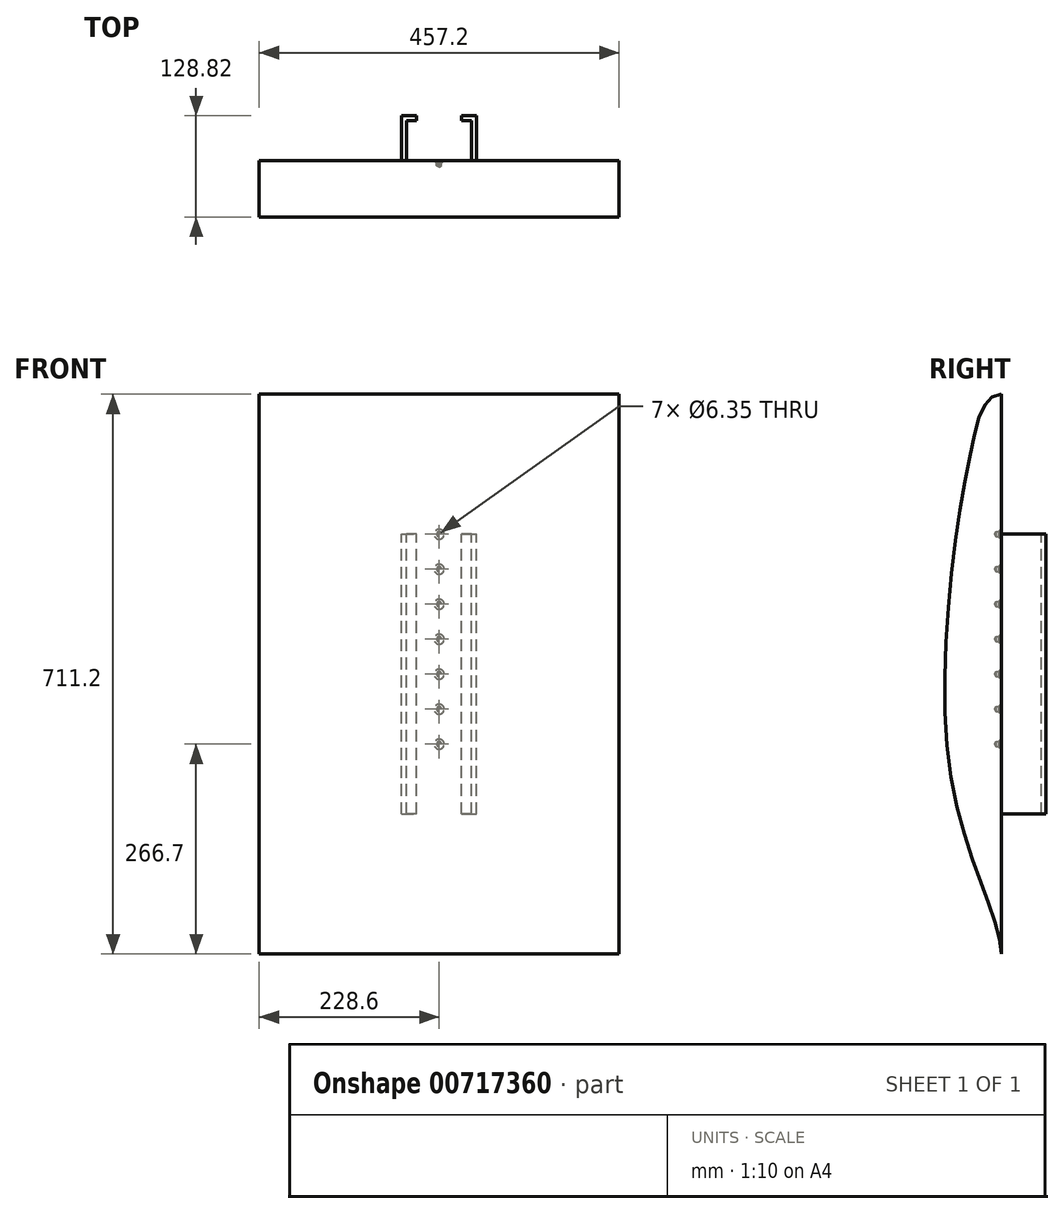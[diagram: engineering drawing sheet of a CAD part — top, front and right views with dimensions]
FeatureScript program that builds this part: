
annotation { "Feature Type Name" : "Feature", "Feature Type Description" : "" }
export const myFeature = defineFeature(function(context is Context, id is Id, definition is map)
    precondition{}
    {
        {
            var Q0;
            Q0=qCreatedBy(makeId("Right.planeOp"),FACE);
            var sketch = newSketch(context, id + "F0", { "sketchPlane" : qUnion([Q0])});
            skLineSegment(sketch, "E0", {"start": v(0, 711.2) * mm, "end": v(0, 0) * mm});
            skFitSpline(sketch, "E1", {"points": [v(0, 711.2) * mm, v(-36.22, 649.45) * mm, v(-62.6, 217.36) * mm, v(0, 0) * mm], "startDerivative": vector(-316.7, 0) * mm, "endDerivative": vector(0, -414.93) * mm});
            skSolve(sketch);
        }
        {
            var Q0;
            Q0=makeQuery(id+"F0.imprint","IMPRINT",FACE,{"disambiguationData":[TD([[makeQuery(id+"F0.imprint","IMPRINT",EDGE,{"derivedFrom":sQuery(id+"F0.wireOp",EDGE,"E0")}),-1.0]])]});
            extrude(context, id + "F1", {"entities" : qUnion([Q0]), "depth" : 457.2 * mm, "offsetDistance" : 25.4 * mm});
        }
        {
            var Q0;
            Q0=makeQuery(id+"F1.opExtrude","SWEPT_FACE",FACE,{"disambiguationData":[OSD([sQuery(id+"F0.wireOp",EDGE,"E0")])]});
            var sketch = newSketch(context, id + "F2", { "sketchPlane" : qUnion([Q0])});
            skLineSegment(sketch, "E2", {"start": v(-228.6, 711.2) * mm, "end": v(-228.6, 0) * mm, "construction": true});
            skLineSegment(sketch, "E3", {"start": v(-457.2, 355.6) * mm, "end": v(0, 355.6) * mm, "construction": true});
            skLineSegment(sketch, "E4.bottom", {"start": v(-180.98, 177.8) * mm, "end": v(-276.23, 177.8) * mm});
            skLineSegment(sketch, "E4.top", {"start": v(-180.98, 533.4) * mm, "end": v(-276.23, 533.4) * mm});
            skLineSegment(sketch, "E4.left", {"start": v(-180.98, 177.8) * mm, "end": v(-180.98, 533.4) * mm});
            skLineSegment(sketch, "E4.right", {"start": v(-276.23, 177.8) * mm, "end": v(-276.23, 533.4) * mm});
            skPoint(sketch, "E4.middle", {"position": v(-228.6, 355.6) * mm});
            skSolve(sketch);
        }
        {
            var Q0;
            Q0=makeQuery(id+"F2.imprint","IMPRINT",FACE,{"disambiguationData":[TD([[makeQuery(id+"F2.imprint","IMPRINT",EDGE,{"derivedFrom":sQuery(id+"F2.wireOp",EDGE,"E4.bottom")}),-1.0]])]});
            extrude(context, id + "F3", {"entities" : qUnion([Q0]), "operationType" : NewBodyOperationType.ADD, "depth" : 57.15 * mm, "offsetDistance" : 25.4 * mm});
        }
        {
            var Q0;
            Q0=makeQuery(id+"F3.opExtrude","SWEPT_FACE",FACE,{"disambiguationData":[OSD([sQuery(id+"F2.wireOp",EDGE,"E4.top")])]});
            var sketch = newSketch(context, id + "F4", { "sketchPlane" : qUnion([Q0])});
            skLineSegment(sketch, "E5", {"start": v(276.23, 57.15) * mm, "end": v(257.18, 57.15) * mm, "construction": true});
            skLineSegment(sketch, "E6", {"start": v(180.98, 57.15) * mm, "end": v(200.03, 57.15) * mm, "construction": true});
            skLineSegment(sketch, "E7", {"start": v(276.23, 0) * mm, "end": v(269.88, 0) * mm, "construction": true});
            skLineSegment(sketch, "E8", {"start": v(180.98, 0) * mm, "end": v(187.33, 0) * mm, "construction": true});
            skLineSegment(sketch, "E9", {"start": v(257.18, 57.15) * mm, "end": v(257.18, 50.8) * mm});
            skLineSegment(sketch, "E10", {"start": v(200.03, 57.15) * mm, "end": v(200.03, 50.8) * mm});
            skLineSegment(sketch, "E11.bottom", {"start": v(269.88, 0) * mm, "end": v(187.33, 0) * mm});
            skLineSegment(sketch, "E11.top", {"start": v(269.88, 50.8) * mm, "end": v(187.33, 50.8) * mm});
            skLineSegment(sketch, "E11.left", {"start": v(269.88, 0) * mm, "end": v(269.88, 50.8) * mm});
            skLineSegment(sketch, "E11.right", {"start": v(187.33, 0) * mm, "end": v(187.33, 50.8) * mm});
            skLineSegment(sketch, "E12", {"start": v(257.18, 57.15) * mm, "end": v(200.03, 57.15) * mm});
            skSolve(sketch);
        }
        {
            var Q0;
            {var subQ0=sQuery(id+"F4.wireOp",EDGE,"E11.left");Q0=makeQuery(id+"F4.imprint","IMPRINT",FACE,{"disambiguationData":[TD([[makeQuery(id+"F4.imprint","IMPRINT",EDGE,{"derivedFrom":subQ0}),1.0]])]});}
            var Q1;
            {var subQ0=sQuery(id+"F4.wireOp",EDGE,"E9");Q1=makeQuery(id+"F4.imprint","IMPRINT",FACE,{"disambiguationData":[TD([[makeQuery(id+"F4.imprint","IMPRINT",EDGE,{"derivedFrom":subQ0}),-1.0]])]});}
            extrude(context, id + "F5", {"entities" : qUnion([Q0, Q1]), "operationType" : NewBodyOperationType.REMOVE, "oppositeDirection" : true, "depth" : 355.6 * mm, "offsetDistance" : 25.4 * mm});
        }
        {
            var Q0;
            Q0=makeQuery(id+"F5.boolean.opBoolean","MERGE",FACE,{"derivedFrom":[makeQuery(id+"F1.opExtrude","SWEPT_FACE",FACE,{"disambiguationData":[OSD([sQuery(id+"F0.wireOp",EDGE,"E0")])]}),makeQuery(id+"F5.opExtrude","SWEPT_FACE",FACE,{"disambiguationData":[OSD([sQuery(id+"F4.wireOp",EDGE,"E11.bottom")])]})]});
            var sketch = newSketch(context, id + "F6", { "sketchPlane" : qUnion([Q0])});
            skLineSegment(sketch, "E13", {"start": v(-276.23, 355.6) * mm, "end": v(-180.98, 355.6) * mm, "construction": true});
            skPoint(sketch, "E14.startSnap0", {"position": v(-228.6, 355.6) * mm});
            skLineSegment(sketch, "E15", {"start": v(-276.23, 533.4) * mm, "end": v(-180.98, 533.4) * mm, "construction": true});
            skLineSegment(sketch, "E16", {"start": v(-276.23, 177.8) * mm, "end": v(-180.98, 177.8) * mm, "construction": true});
            skLineSegment(sketch, "E17", {"start": v(-276.23, 355.6) * mm, "end": v(-276.23, 177.8) * mm, "construction": true});
            skLineSegment(sketch, "E18", {"start": v(-276.23, 266.7) * mm, "end": v(-180.98, 266.7) * mm, "construction": true});
            skLineSegment(sketch, "E19", {"start": v(-276.23, 355.6) * mm, "end": v(-276.23, 533.4) * mm, "construction": true});
            skLineSegment(sketch, "E20", {"start": v(-276.23, 444.5) * mm, "end": v(-180.98, 444.5) * mm, "construction": true});
            skLineSegment(sketch, "E21", {"start": v(-180.98, 533.4) * mm, "end": v(-180.98, 444.5) * mm, "construction": true});
            skLineSegment(sketch, "E22", {"start": v(-180.98, 488.95) * mm, "end": v(-276.23, 488.95) * mm, "construction": true});
            skLineSegment(sketch, "E23", {"start": v(-180.98, 444.5) * mm, "end": v(-180.98, 355.6) * mm, "construction": true});
            skLineSegment(sketch, "E24", {"start": v(-180.98, 400.05) * mm, "end": v(-276.23, 400.05) * mm, "construction": true});
            skLineSegment(sketch, "E25", {"start": v(-180.98, 355.6) * mm, "end": v(-180.98, 266.7) * mm, "construction": true});
            skLineSegment(sketch, "E26", {"start": v(-180.98, 311.15) * mm, "end": v(-276.23, 311.15) * mm, "construction": true});
            skLineSegment(sketch, "E27", {"start": v(-180.98, 266.7) * mm, "end": v(-180.98, 177.8) * mm, "construction": true});
            skPoint(sketch, "E28", {"position": v(-228.6, 488.95) * mm});
            skPoint(sketch, "E29", {"position": v(-228.6, 400.05) * mm});
            skPoint(sketch, "E30", {"position": v(-228.6, 444.5) * mm});
            skPoint(sketch, "E31", {"position": v(-228.6, 311.15) * mm});
            skPoint(sketch, "E32", {"position": v(-228.6, 266.7) * mm});
            skPoint(sketch, "E33", {"position": v(-228.6, 533.4) * mm});
            skSolve(sketch);
        }
        {
            var Q0;
            Q0=sQuery(id+"F6.wireOp",VERTEX,"E33");
            var Q1;
            Q1=sQuery(id+"F6.wireOp",VERTEX,"E28");
            var Q2;
            Q2=sQuery(id+"F6.wireOp",VERTEX,"E30");
            var Q3;
            Q3=sQuery(id+"F6.wireOp",VERTEX,"E29");
            var Q4;
            Q4=sQuery(id+"F6.wireOp",VERTEX,"E14.startSnap0");
            var Q5;
            Q5=sQuery(id+"F6.wireOp",VERTEX,"E31");
            var Q6;
            Q6=sQuery(id+"F6.wireOp",VERTEX,"E32");
            var Q7;
            Q7=makeQuery(id+"F1.opExtrude","SWEPT_BODY",BODY,{"disambiguationData":[OSD([sQuery(id+"F0.wireOp",EDGE,"E0"),sQuery(id+"F0.wireOp",EDGE,"E1")])]});
            hole(context, id + "F7", {"style" : HoleStyle.C_SINK, "endStyle" : HoleEndStyle.BLIND, "holeDiameter" : 6.35 * mm, "cSinkDiameter" : 12.7 * mm, "cSinkAngle" : 90 * degree, "majorDiameter" : 6.35 * mm, "holeDepth" : 6.35 * mm, "isTappedThrough" : true, "tappedDepth" : 12.7 * mm, "tapClearance" : 3, "locations" : qUnion([Q0, Q1, Q2, Q3, Q4, Q5, Q6]), "scope" : qUnion([Q7])});
        }
    });
